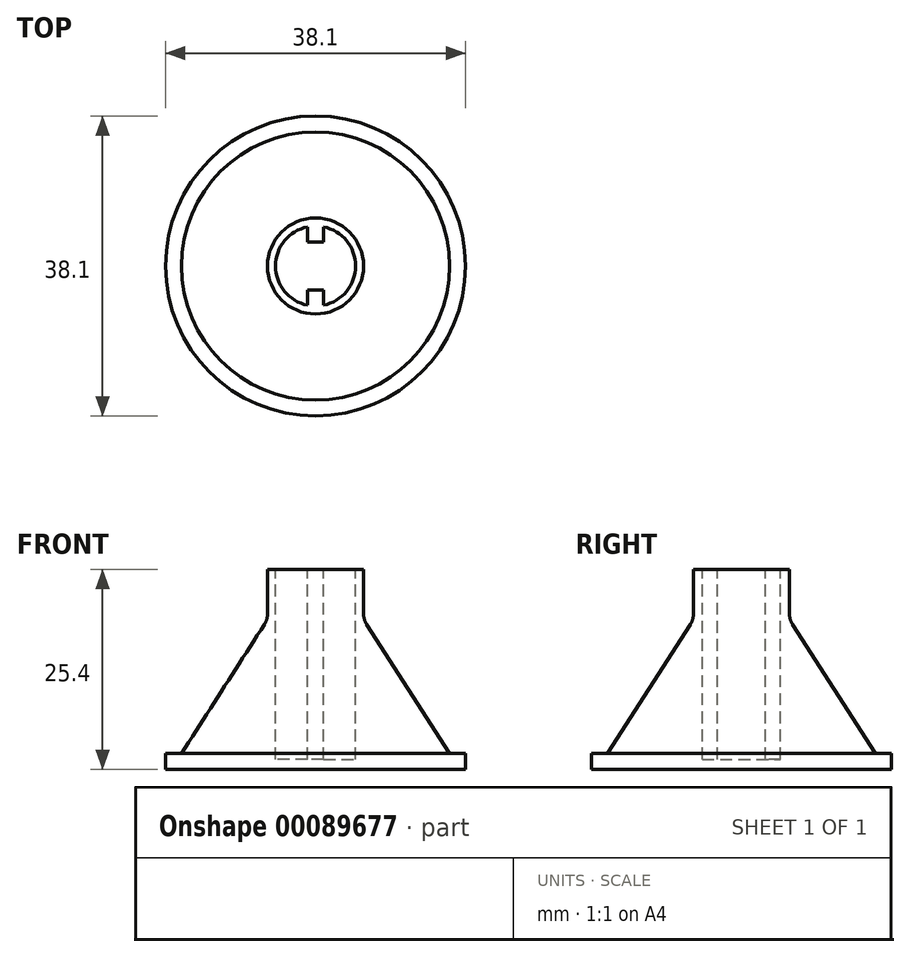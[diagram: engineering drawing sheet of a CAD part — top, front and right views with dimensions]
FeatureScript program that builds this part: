
annotation { "Feature Type Name" : "Feature", "Feature Type Description" : "" }
export const myFeature = defineFeature(function(context is Context, id is Id, definition is map)
    precondition{}
    {
        {
            var Q0;
            Q0=qCreatedBy(makeId("Front.planeOp"),FACE);
            var sketch = newSketch(context, id + "F0", { "sketchPlane" : qUnion([Q0])});
            skLineSegment(sketch, "E0", {"start": v(0, 0) * mm, "end": v(0, 19.05) * mm});
            skLineSegment(sketch, "E1", {"start": v(0, 19.05) * mm, "end": v(6.1, 19.05) * mm});
            skLineSegment(sketch, "E2", {"start": v(19.05, 0) * mm, "end": v(0, 0) * mm});
            skLineSegment(sketch, "E3.left", {"start": v(0, 19.05) * mm, "end": v(0, 19.05) * mm});
            skLineSegment(sketch, "E3.right", {"start": v(6.1, 19.05) * mm, "end": v(6.1, 19.05) * mm});
            skLineSegment(sketch, "E4.top", {"start": v(0, 25.4) * mm, "end": v(6.1, 25.4) * mm});
            skLineSegment(sketch, "E4.left", {"start": v(0, 19.05) * mm, "end": v(0, 25.4) * mm});
            skLineSegment(sketch, "E4.right", {"start": v(6.1, 19.05) * mm, "end": v(6.1, 25.4) * mm});
            skLineSegment(sketch, "E5", {"start": v(19.05, 0) * mm, "end": v(19.05, 2.03) * mm});
            skLineSegment(sketch, "E6", {"start": v(19.05, 2.03) * mm, "end": v(17.02, 2.03) * mm});
            skLineSegment(sketch, "E7", {"start": v(17.02, 2.03) * mm, "end": v(6.1, 19.05) * mm});
            skSolve(sketch);
        }
        {
            var Q0;
            Q0 = qSketchRegion(id + "F0", true);
            var Q1;
            Q1=sQuery(id+"F0.wireOp",EDGE,"E0");
            revolve(context, id + "F1", {"entities" : qUnion([Q0]), "axis" : qUnion([Q1]), "revolveType" : RevolveType.FULL});
        }
        {
            var Q0;
            Q0=makeQuery(id+"F1.opRevolve","SWEPT_FACE",FACE,{"disambiguationData":[OSD([sQuery(id+"F0.wireOp",EDGE,"E4.top")])]});
            var sketch = newSketch(context, id + "F2", { "sketchPlane" : qUnion([Q0])});
            skCircle(sketch, "E8", {"center": v(0, 0) * mm, "radius": 5.08 * mm});
            skSolve(sketch);
        }
        {
            var Q0;
            Q0 = qSketchRegion(id + "F2", true);
            extrude(context, id + "F3", {"entities" : qUnion([Q0]), "operationType" : NewBodyOperationType.REMOVE, "oppositeDirection" : true, "depth" : 24.13 * mm});
        }
        {
            var Q0;
            Q0=makeQuery(id+"F1.opRevolve","SWEPT_EDGE",EDGE,{"disambiguationData":[OSD([sQuery(id+"F0.wireOp",EDGE,"99Yukjws-nxL6-M9vy-GY2z-gxU8x74I4FID"),sQuery(id+"F0.wireOp",EDGE,"E1"),sQuery(id+"F0.wireOp",EDGE,"E4.right")])]});
            fillet(context, id + "F4", {"entities" : qUnion([Q0]), "radius" : 2.54 * mm, "tangentPropagation" : true, "allowEdgeOverflow" : false});
        }
        {
            var Q0;
            Q0=makeQuery(id+"F1.opRevolve","SWEPT_FACE",FACE,{"disambiguationData":[OSD([sQuery(id+"F0.wireOp",EDGE,"E4.top")])]});
            var sketch = newSketch(context, id + "F5", { "sketchPlane" : qUnion([Q0])});
            skLineSegment(sketch, "E9.bottom", {"start": v(1.02, -5.59) * mm, "end": v(-1.02, -5.59) * mm});
            skLineSegment(sketch, "E9.top", {"start": v(1.02, -3.05) * mm, "end": v(-1.02, -3.05) * mm});
            skLineSegment(sketch, "E9.left", {"start": v(1.02, -5.59) * mm, "end": v(1.02, -3.05) * mm});
            skLineSegment(sketch, "E9.right", {"start": v(-1.02, -5.59) * mm, "end": v(-1.02, -3.05) * mm});
            skPoint(sketch, "E9.middle", {"position": v(0, -4.32) * mm});
            skLineSegment(sketch, "E10.bottom", {"start": v(-1.02, 5.59) * mm, "end": v(1.02, 5.59) * mm});
            skLineSegment(sketch, "E10.top", {"start": v(-1.02, 3.05) * mm, "end": v(1.02, 3.05) * mm});
            skLineSegment(sketch, "E10.left", {"start": v(-1.02, 5.59) * mm, "end": v(-1.02, 3.05) * mm});
            skLineSegment(sketch, "E10.right", {"start": v(1.02, 5.59) * mm, "end": v(1.02, 3.05) * mm});
            skPoint(sketch, "E10.middle", {"position": v(0, 4.32) * mm});
            skSolve(sketch);
        }
        {
            var Q0;
            Q0 = qSketchRegion(id + "F5", true);
            extrude(context, id + "F6", {"entities" : qUnion([Q0]), "operationType" : NewBodyOperationType.ADD, "oppositeDirection" : true, "depth" : 25.4 * mm});
        }
    });
